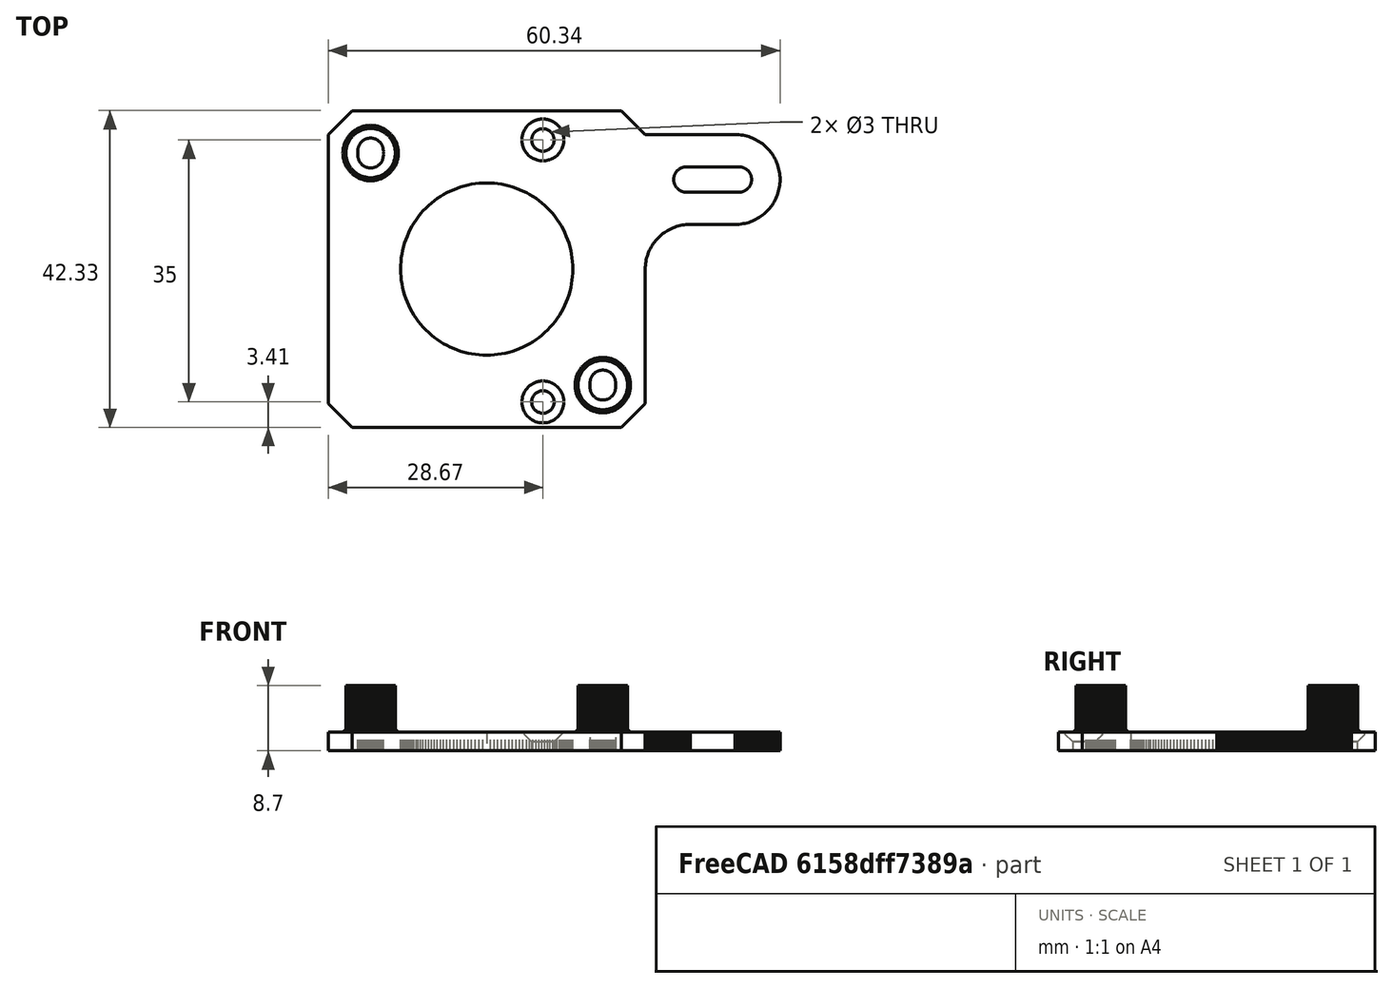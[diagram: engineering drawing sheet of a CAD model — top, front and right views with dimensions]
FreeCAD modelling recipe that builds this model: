
FCSTD DOCUMENT  (FreeCAD 0.20R)
Label: motor_spacer_small
License: All rights reserved
LicenseURL: http://en.wikipedia.org/wiki/All_rights_reserved
objects: Part::Feature×2, Mesh::Feature×1, PartDesign::FeatureBase×1, Sketcher::SketchObject×1, PartDesign::Pocket×1, PartDesign::Line×1, PartDesign::Chamfer×1, PartDesign::Body×1
note: 10 computed .brp shape members not serialized (recipe doc carries the construction recipe); baked Part::Feature solids carry a one-line shape summary decoded from their .brp

FEATURE [Mesh::Feature] motor_spacer  label="motor-spacer"
FEATURE [Part::Feature] motor_spacer001
  shape: bbox 60.33 x 42.33 x 8.7 mm, 4684 faces, 0 solids (baked)
FEATURE [Part::Feature] motor_spacer001_solid  label="motor_spacer001 (Solid)"
  shape: bbox 60.33 x 42.33 x 8.7 mm, 4684 faces (baked)
FEATURE [PartDesign::FeatureBase] BaseFeature
  BaseFeature = -> motor_spacer001_solid
FEATURE [Sketcher::SketchObject] Sketch
  FullyConstrained = true
  MapMode = 5
  Support = -> [XY_Plane]
  sketch-geometry (2):
    g0: Circle CenterX=-1.5 CenterY=17.25 CenterZ=0 NormalX=0 NormalY=0 NormalZ=1 AngleXU=0 Radius=1.5
    g1: Circle CenterX=-1.5 CenterY=-17.75 CenterZ=0 NormalX=0 NormalY=0 NormalZ=1 AngleXU=0 Radius=1.5
  constraints (6):
    c: Equal(g0,g1)
    c: Diameter(g0) = 3
    c: Distance(g0,g1) = 35
    c: DistanceY(g-1,g0) = 17.25
    c: DistanceX(g-2,g0) = -1.5
    c: DistanceX(g-2,g1) = -1.5
FEATURE [PartDesign::Pocket] Pocket
  BaseFeature = -> BaseFeature
  Direction = (0,0,-1)
  Length = 5
  Length2 = 5
  Profile = -> Sketch
  ReferenceAxis = -> Sketch [N_Axis]
  Reversed = true
  Type = 0
FEATURE [PartDesign::Line] DatumLine
  AttacherType = Attacher::AttachEngineLine
  AttachmentOffset = pos=(-9.5,0,0) rot=(0,0,1;0rad)
  Length = 20
  MapMode = 17
  Placement = pos=(-9.5,0,0) rot=(1,0,0;1.5708rad)
  ResizeMode = 0
  Support = -> [Sketch]
FEATURE [PartDesign::Chamfer] Chamfer
  Angle = 45
  Base = -> Pocket [Edge2074,Edge2390,Edge2584,Edge2585,Edge2586,Edge2587,Edge2588,Edge2589,Edge2590,Edge2591,Edge2592,Edge2593,Edge2594,Edge2595,Edge2596,Edge2597,Edge2598,Edge2599,Edge2600,Edge2601,Edge2602,Edge2583,Edge2582,Edge2581,Edge2580,Edge2579,Edge2578,Edge2577,Edge2576,Edge2575,Edge2574,Edge2573,Edge2572,Edge2571,Edge2570,Edge2569,Edge2568,Edge2567,Edge2563]
  BaseFeature = -> Pocket
  ChamferType = 0
  FlipDirection = false
  Size = 1.3
  Size2 = 1
  SupportTransform = false
  UseAllEdges = false
FEATURE [PartDesign::Body] Body
  BaseFeature = -> motor_spacer001_solid
  Group = -> [BaseFeature,Sketch,Pocket,DatumLine,Chamfer]
  Origin = -> Origin
  Tip = -> Chamfer
